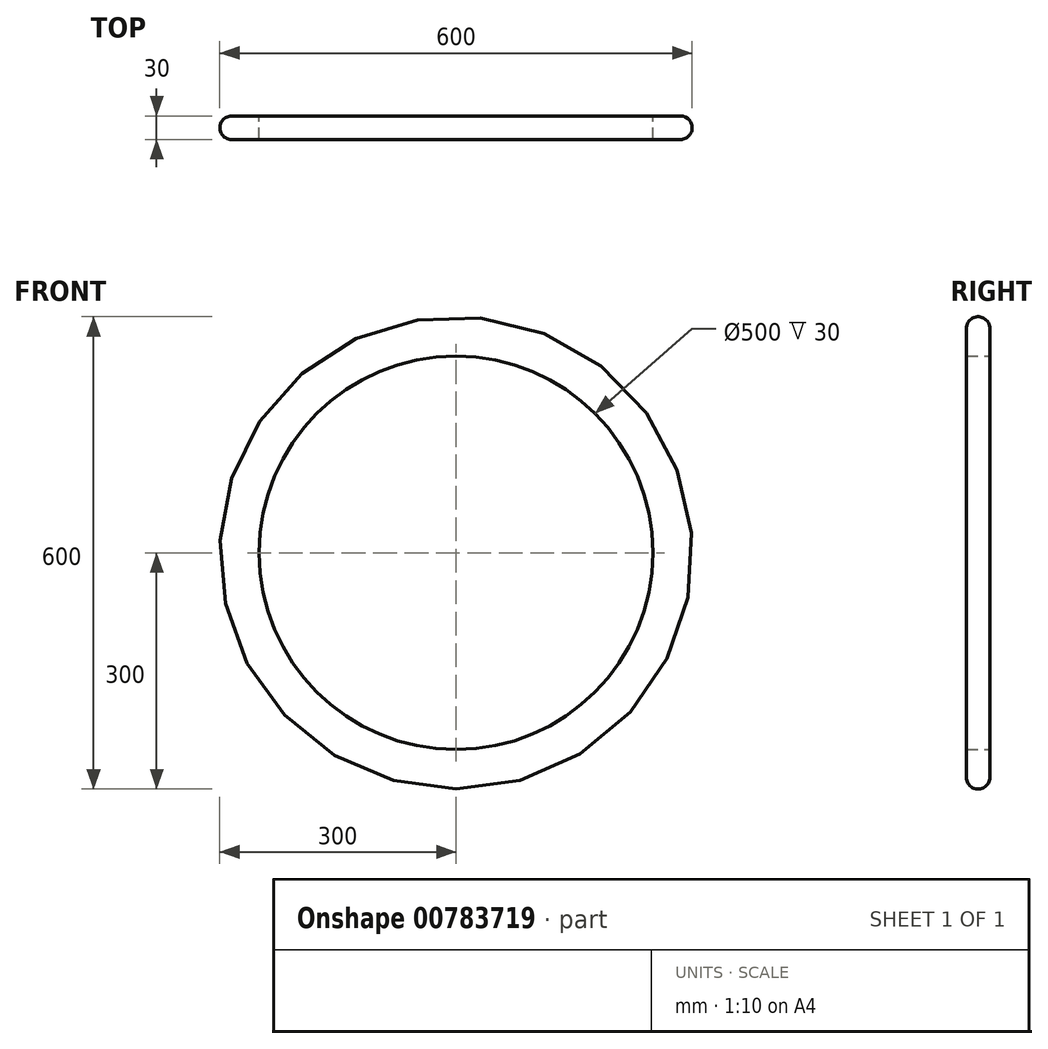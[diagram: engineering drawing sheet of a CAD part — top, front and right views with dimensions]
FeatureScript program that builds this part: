
annotation { "Feature Type Name" : "Feature", "Feature Type Description" : "" }
export const myFeature = defineFeature(function(context is Context, id is Id, definition is map)
    precondition{}
    {
        {
            var Q0;
            Q0=qCreatedBy(makeId("Front.planeOp"),FACE);
            var sketch = newSketch(context, id + "F0", { "sketchPlane" : qUnion([Q0])});
            skCircle(sketch, "E0", {"center": v(0, 0) * mm, "radius": 300 * mm});
            skCircle(sketch, "E1.0", {"center": v(0, 0) * mm, "radius": 250 * mm});
            skSolve(sketch);
        }
        {
            var Q0;
            Q0=makeQuery(id+"F0.imprint","IMPRINT",FACE,{"disambiguationData":[TD([[makeQuery(id+"F0.imprint","IMPRINT",EDGE,{"derivedFrom":sQuery(id+"F0.wireOp",EDGE,"E0")}),1.0]])]});
            extrude(context, id + "F1", {"entities" : qUnion([Q0]), "depth" : 30 * mm, "offsetDistance" : 25 * mm});
        }
        {
            var Q0;
            Q0=makeQuery(id+"F1.opExtrude","SWEPT_FACE",FACE,{"disambiguationData":[OSD([sQuery(id+"F0.wireOp",EDGE,"E0")])]});
            fillet(context, id + "F2", {"entities" : qUnion([Q0]), "radius" : 15 * mm, "tangentPropagation" : true, "allowEdgeOverflow" : false});
        }
    });
